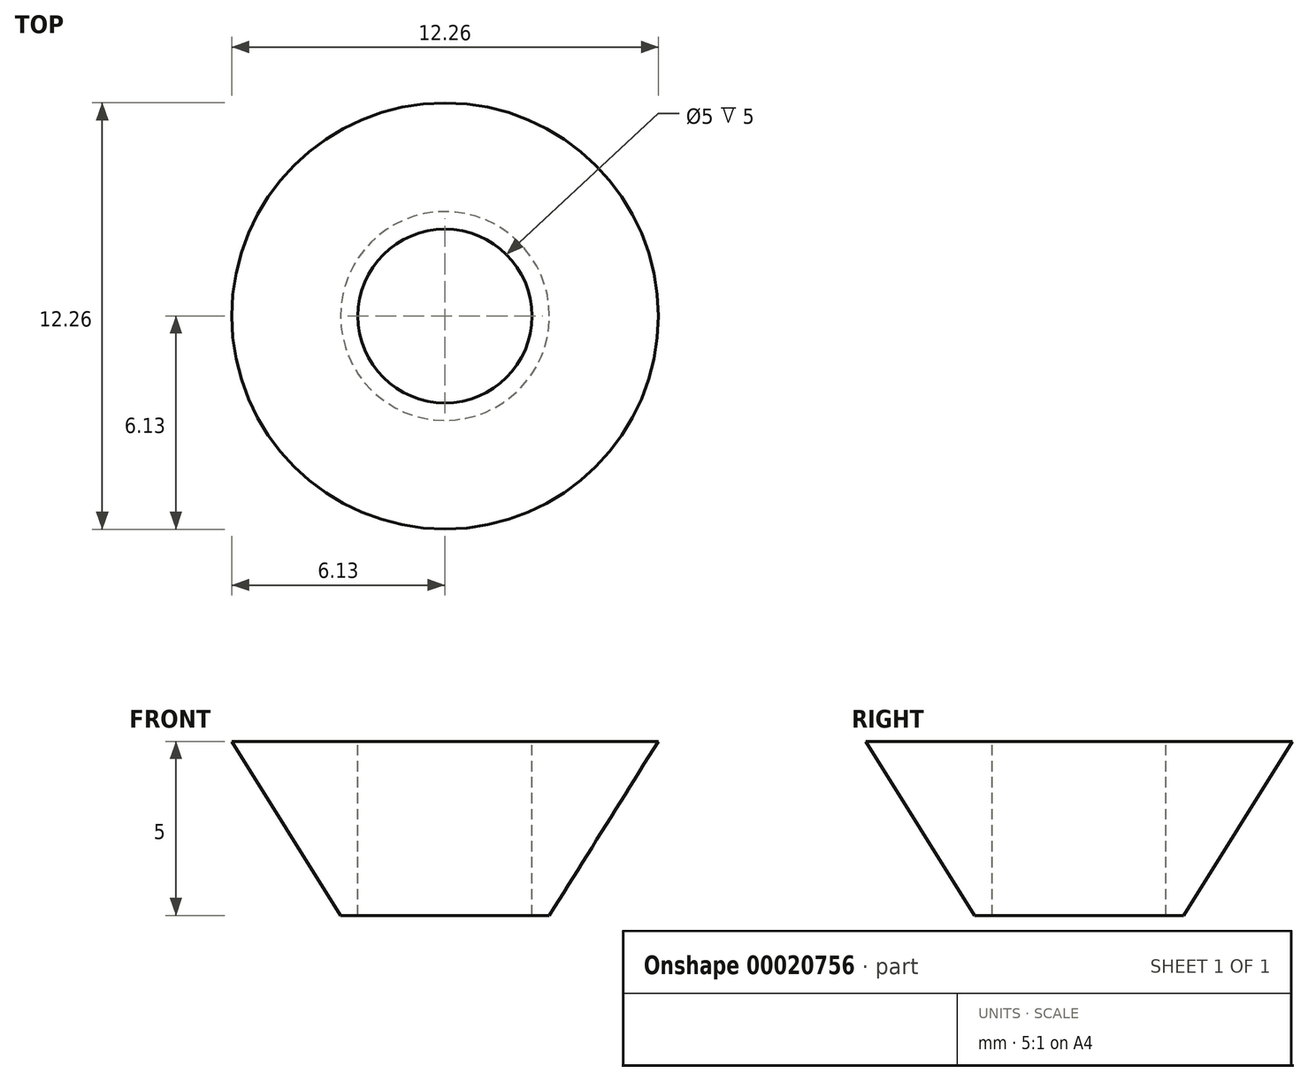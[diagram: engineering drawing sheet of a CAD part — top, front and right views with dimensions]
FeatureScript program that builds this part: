
annotation { "Feature Type Name" : "Feature", "Feature Type Description" : "" }
export const myFeature = defineFeature(function(context is Context, id is Id, definition is map)
    precondition{}
    {
        {
            var Q0;
            Q0=qCreatedBy(makeId("Top.planeOp"),FACE);
            var sketch = newSketch(context, id + "F0", { "sketchPlane" : qUnion([Q0])});
            skCircle(sketch, "E0", {"center": v(0, 0) * mm, "radius": 2.5 * mm});
            skCircle(sketch, "E1", {"center": v(0, 0) * mm, "radius": 6.12 * mm});
            skSolve(sketch);
        }
        {
            var Q0;
            Q0=qCreatedBy(makeId("Front.planeOp"),FACE);
            var sketch = newSketch(context, id + "F1", { "sketchPlane" : qUnion([Q0])});
            skLineSegment(sketch, "E2", {"start": v(6.12, 0) * mm, "end": v(3, -5) * mm});
            skLineSegment(sketch, "E3", {"start": v(3, -5) * mm, "end": v(2.5, -5) * mm});
            skLineSegment(sketch, "E4", {"start": v(2.5, -5) * mm, "end": v(2.5, 0) * mm});
            skLineSegment(sketch, "E5", {"start": v(2.5, 0) * mm, "end": v(6.12, 0) * mm});
            skSolve(sketch);
        }
        {
            var Q0;
            Q0=makeQuery(id+"F1.imprint","IMPRINT",FACE,{"disambiguationData":[TD([[makeQuery(id+"F1.imprint","IMPRINT",EDGE,{"derivedFrom":sQuery(id+"F1.wireOp",EDGE,"E2")}),-1.0]])]});
            var Q1;
            Q1=sQuery(id+"F0.wireOp",EDGE,"E0");
            sweep(context, id + "F2", {"profiles" : qUnion([Q0]), "path" : qUnion([Q1])});
        }
    });
